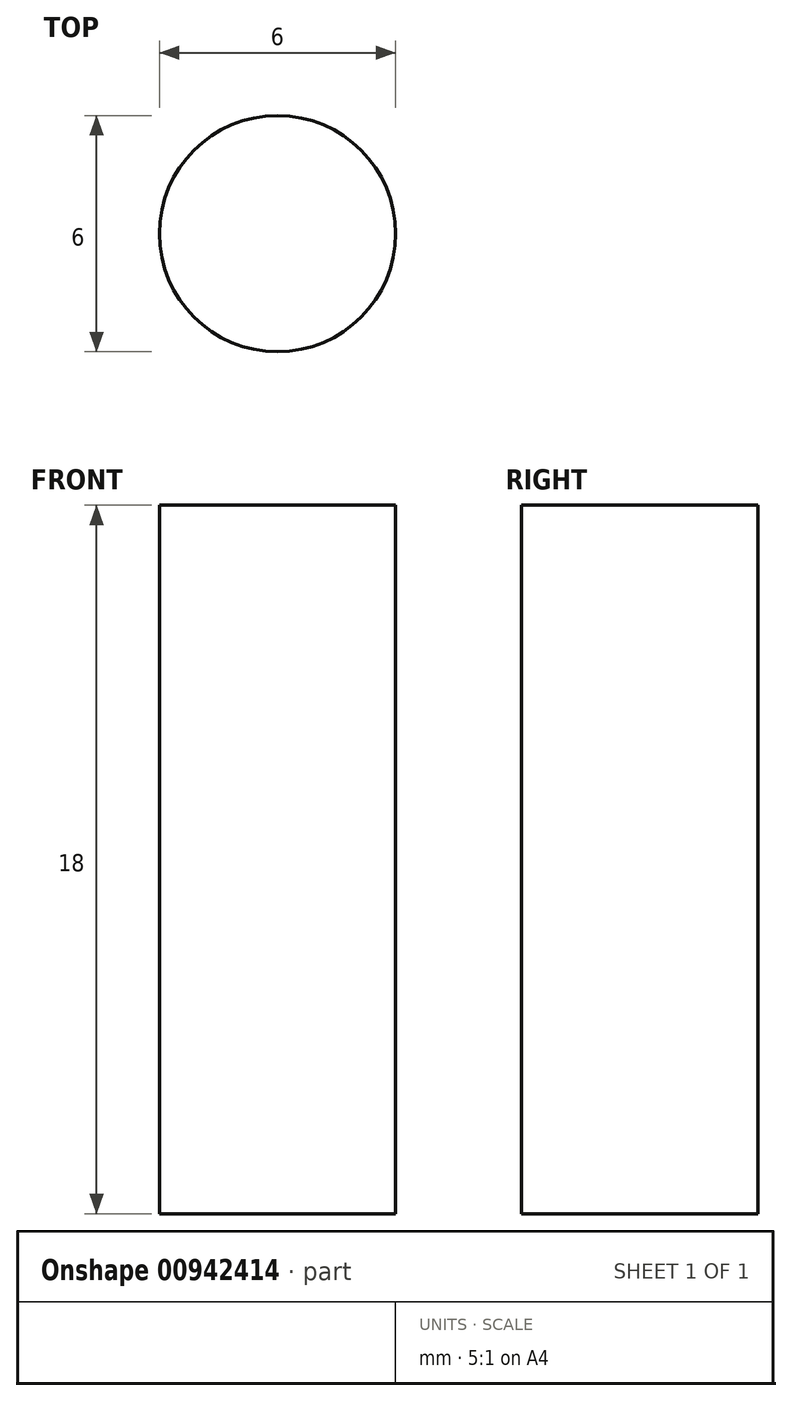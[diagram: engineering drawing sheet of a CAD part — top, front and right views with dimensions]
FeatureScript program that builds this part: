
annotation { "Feature Type Name" : "Feature", "Feature Type Description" : "" }
export const myFeature = defineFeature(function(context is Context, id is Id, definition is map)
    precondition{}
    {
        {
            var Q0;
            Q0=qCreatedBy(makeId("Top.planeOp"),FACE);
            var sketch = newSketch(context, id + "F0", { "sketchPlane" : qUnion([Q0])});
            skCircle(sketch, "E0", {"center": v(0, 0) * mm, "radius": 3 * mm});
            skSolve(sketch);
        }
        {
            var Q0;
            Q0=makeQuery(id+"F0.imprint","IMPRINT",FACE,{"disambiguationData":[TD([[makeQuery(id+"F0.imprint","IMPRINT",EDGE,{"derivedFrom":sQuery(id+"F0.wireOp",EDGE,"E0")}),1.0]])]});
            extrude(context, id + "F1", {"entities" : qUnion([Q0]), "depth" : 18 * mm, "offsetDistance" : 25 * mm});
        }
    });
